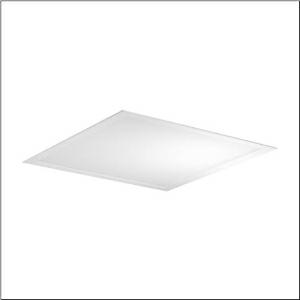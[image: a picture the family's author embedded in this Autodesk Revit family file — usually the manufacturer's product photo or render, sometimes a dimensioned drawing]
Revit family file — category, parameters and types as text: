
# Revit family: apollon_21_square_51mq11w72414
name_source: partatom
category: Lighting Fixtures
units: mm (PartAtom-declared; Revit-internal decimal feet)

## family parameters
Cut with Voids When Loaded = No
Host = Face
Light Source = No
Part Type = Normal
Room Calculation Point = No
Round Connector Dimension = Use Diameter
Shared = No

## types (1)
- Apollon 21 square (1 x LED, 4200 lm, 23.3 W, 4000K)
    Apparent Load = 23 VA
    CIE Flux Codes = 60 87 97 100 100
    Color Rendering = 80
    Color Temperature = 4000K
    Default Elevation = 1800 mm
    Description = Apollon 21 square, office luminaire, primary optical cover: micro prismatic cover, of PMMA, CAT 2 (L<= 3000cd/m²), light emission: direct distribution, primary light characteristic: symmetric, installation type: lay-in mounting, LED, rated luminous flux: 4.200lm, luminous efficacy: 180lm/W, light colour: 840, colour temperature: 4000K, control gear: ON/OFF, with terminal, 3-pole, mains connection: 220..240V, AC/DC, 0/50..60Hz, rated input power: 23.3W, suitable for self-contained emergency lighting element 59MQE002602A with integrated self-test function according to EN 60598-2-22, housing, of aluminium, coated, traffic white (RAL 9016), module: M625, length: 620mm, width: 620mm, height: 55mm, recess depth: 180mm, housing upper side, of sheet steel, galvanised, protection rating (complete): IP20, protection rating (lamp compartment, on room side): IP50, insulation class (complete): insulation class II (safety insulation), certification: CE, ENEC, impact resistance: IK03, permissible operating ambient temperature: -20..+45°C, permissible storage temperature: -40..+80°C, standard: EN 60598-2-22, packaging unit: 1 piece
    Height = 0 mm  [stored 0 ft]
    Lamp = 1 x LED
    Lamp Light Flux = 4200 lm
    Lamp Power = 23.3 W
    Lamp count = 1
    Length = 620 mm
    Luminous efficacy = 180 lm/W
    Manufacturer = Siteco
    ModVariant = No
    Model = 51MQ11W72414
    Mounting Place = Ceiling
    Mounting Type = Recessed
    Number of Poles = 1
    OnlyDefault = Yes
    Power Factor = 1
    Product Name = Apollon 21 square
    Product group = office luminaire | ceiling recessed
    ProductGroupID = 400
    Protection Class = Protection class II
    Protection Degree = IP 20
    RLX_Detail_Level = 1
    RLX_Emergency_Light_Flux = 0 lm
    RLX_Emergency_Type = 0
    RLX_Emergency_Type_DB = No
    RlxData = <blob elided: 13161 chars, md5=426c79be>
    Socket = socket
    Standby Power = 0 W
    System Light Flux = 4200 lm
    System Power = 23 W
    Type Comments = Product without accessories
    Type Image = l_1291054.jpg
    URL = http://relux.com
    VarID = ---
    Voltage = 0 V
    Weight = 0.00 kg
    Width = 620 mm

note: [stored X ft] marks values corroborated as IEEE doubles in the binary element streams (Revit-internal decimal feet)

## geometry (parser evidence)
native form markers: Sweep x9
no freeform markers — native parametric forms only
